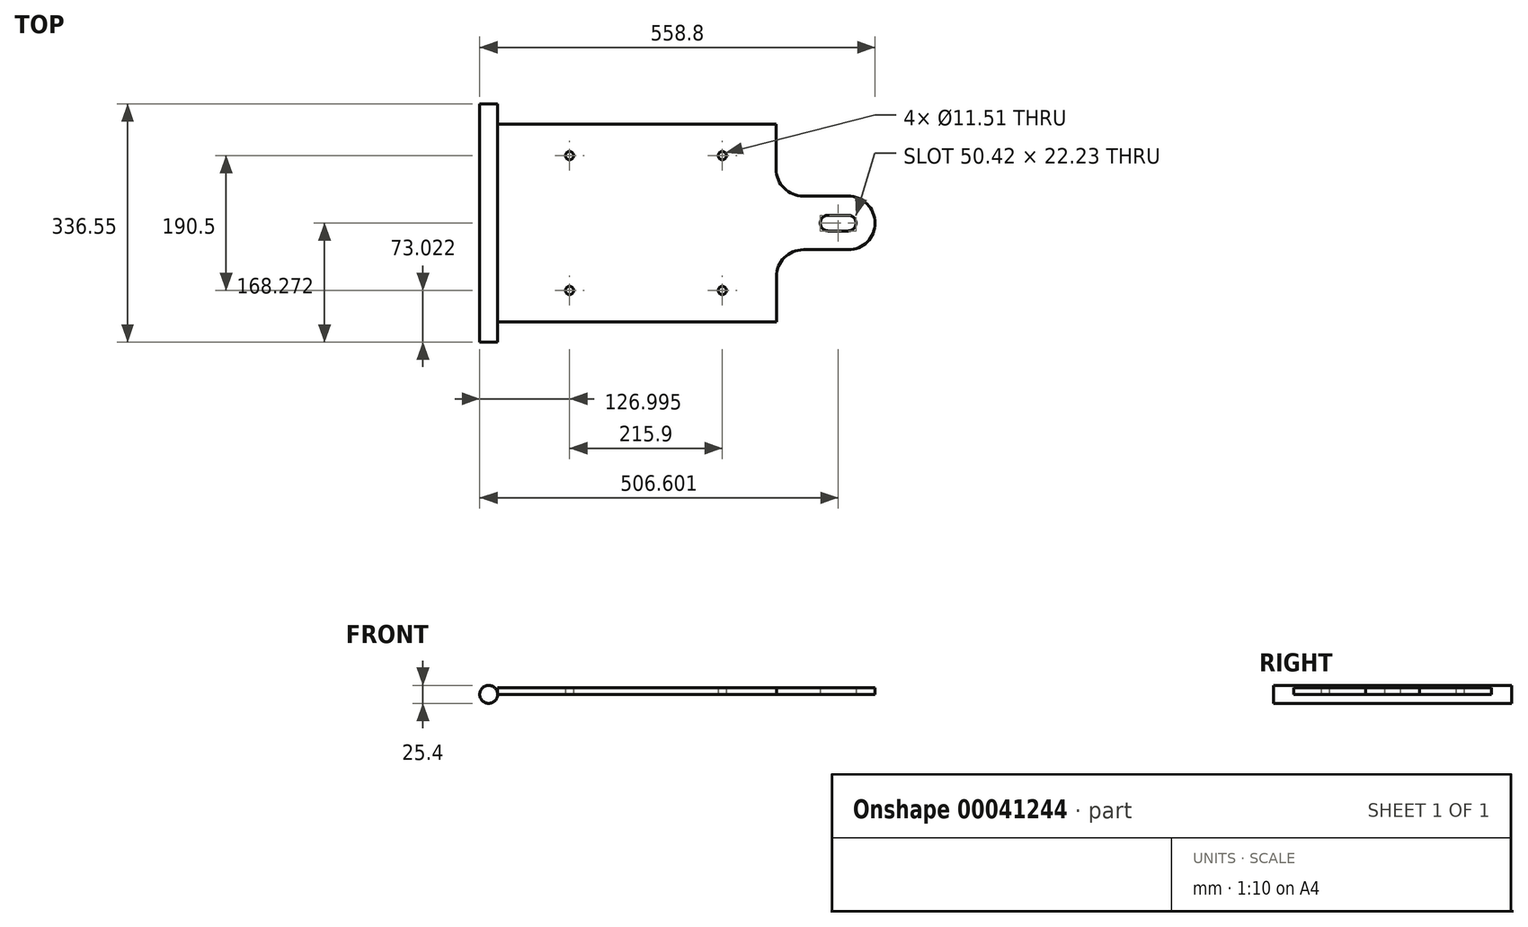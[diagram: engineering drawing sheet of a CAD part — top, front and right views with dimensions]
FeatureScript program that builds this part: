
annotation { "Feature Type Name" : "Feature", "Feature Type Description" : "" }
export const myFeature = defineFeature(function(context is Context, id is Id, definition is map)
    precondition{}
    {
        {
            var Q0;
            Q0=qCreatedBy(makeId("Top.planeOp"),FACE);
            var sketch = newSketch(context, id + "F0", { "sketchPlane" : qUnion([Q0])});
            skLineSegment(sketch, "E0.bottom", {"start": v(-236.93, 236.13) * mm, "end": v(156.77, 236.13) * mm});
            skLineSegment(sketch, "E0.top", {"start": v(-236.93, -43.27) * mm, "end": v(157.15, -43.27) * mm});
            skLineSegment(sketch, "E0.left", {"start": v(-236.93, 236.13) * mm, "end": v(-236.93, -43.27) * mm});
            skLineSegment(sketch, "E1", {"start": v(-236.93, 96.43) * mm, "end": v(296.47, 96.43) * mm, "construction": true});
            skPoint(sketch, "E1.startSnap0", {"position": v(-236.93, 96.43) * mm});
            skLineSegment(sketch, "E2", {"start": v(-236.93, 236.13) * mm, "end": v(-135.33, 236.13) * mm});
            skLineSegment(sketch, "E3", {"start": v(-135.33, 236.13) * mm, "end": v(80.57, 236.13) * mm, "construction": true});
            skLineSegment(sketch, "E4", {"start": v(-135.33, 236.13) * mm, "end": v(80.57, 236.13) * mm});
            skLineSegment(sketch, "E5.rect.bottom", {"start": v(80.57, 1.18) * mm, "end": v(-135.33, 1.18) * mm, "construction": true});
            skLineSegment(sketch, "E5.rect.top", {"start": v(80.57, 191.68) * mm, "end": v(-135.33, 191.68) * mm, "construction": true});
            skLineSegment(sketch, "E5.rect.left", {"start": v(80.57, 1.18) * mm, "end": v(80.57, 191.68) * mm, "construction": true});
            skLineSegment(sketch, "E5.rect.right", {"start": v(-135.33, 1.18) * mm, "end": v(-135.33, 191.68) * mm, "construction": true});
            skPoint(sketch, "E5.rect.middle", {"position": v(-27.38, 96.43) * mm});
            skLineSegment(sketch, "E6", {"start": v(156.77, 236.13) * mm, "end": v(156.77, 172.63) * mm});
            skLineSegment(sketch, "E7.rect.bottom", {"start": v(194.87, 134.53) * mm, "end": v(258.37, 134.53) * mm});
            skLineSegment(sketch, "E7.rect.top", {"start": v(195.25, 58.72) * mm, "end": v(258.75, 58.72) * mm});
            skLineSegment(sketch, "E8", {"start": v(-135.33, 191.68) * mm, "end": v(-135.33, 236.13) * mm, "construction": true});
            skLineSegment(sketch, "E9", {"start": v(-135.33, 1.18) * mm, "end": v(-135.33, -43.27) * mm, "construction": true});
            skArc(sketch, "E10.filletArc", {"start": v(156.77, 172.63) * mm, "mid": v(167.92, 145.7) * mm, "end": v(194.87, 134.53) * mm});
            skLineSegment(sketch, "E11", {"start": v(157.15, 20.62) * mm, "end": v(157.15, -43.27) * mm});
            skArc(sketch, "E12.filletArc", {"start": v(195.25, 58.72) * mm, "mid": v(168.3, 47.56) * mm, "end": v(157.15, 20.62) * mm});
            skLineSegment(sketch, "E13", {"start": v(296.47, 96.43) * mm, "end": v(296.47, 96.43) * mm});
            skArc(sketch, "E14.filletArc", {"start": v(296.47, 96.43) * mm, "mid": v(285.3, 123.37) * mm, "end": v(258.37, 134.53) * mm});
            skArc(sketch, "E15.filletArc", {"start": v(258.75, 58.72) * mm, "mid": v(285.42, 69.76) * mm, "end": v(296.47, 96.43) * mm});
            skLineSegment(sketch, "E16", {"start": v(258.37, 96.43) * mm, "end": v(230.18, 96.43) * mm});
            skArc(sketch, "E17.0.startCap", {"start": v(258.37, 107.54) * mm, "mid": v(269.48, 96.43) * mm, "end": v(258.37, 85.32) * mm});
            skArc(sketch, "E17.0.endCap", {"start": v(230.18, 85.32) * mm, "mid": v(219.06, 96.43) * mm, "end": v(230.18, 107.54) * mm});
            skLineSegment(sketch, "E17.0.left", {"start": v(258.37, 85.32) * mm, "end": v(230.18, 85.32) * mm});
            skLineSegment(sketch, "E17.0.right", {"start": v(258.37, 107.54) * mm, "end": v(230.18, 107.54) * mm});
            skPoint(sketch, "E18", {"position": v(296.47, 96.43) * mm});
            skSolve(sketch);
        }
        {
            var Q0;
            Q0=makeQuery(id+"F0.imprint","IMPRINT",FACE,{"disambiguationData":[TD([[makeQuery(id+"F0.imprint","IMPRINT",EDGE,{"derivedFrom":sQuery(id+"F0.wireOp",EDGE,"E0.bottom")}),-1.0]])]});
            extrude(context, id + "F1", {"entities" : qUnion([Q0]), "depth" : 9.52 * mm});
        }
        {
            var Q0;
            Q0=sQuery(id+"F0.wireOp",VERTEX,"E5.rect.right.end");
            var Q1;
            Q1=sQuery(id+"F0.wireOp",VERTEX,"E5.rect.top.start");
            var Q2;
            Q2=sQuery(id+"F0.wireOp",VERTEX,"E5.rect.bottom.start");
            var Q3;
            Q3=sQuery(id+"F0.wireOp",VERTEX,"E5.rect.bottom.end");
            var Q4;
            Q4=makeQuery(id+"F1.opExtrude","SWEPT_BODY",BODY,{"disambiguationData":[OSD([sQuery(id+"F0.wireOp",EDGE,"E0.bottom"),sQuery(id+"F0.wireOp",EDGE,"E0.top"),sQuery(id+"F0.wireOp",EDGE,"E0.left"),sQuery(id+"F0.wireOp",EDGE,"E0.right"),sQuery(id+"F0.wireOp",EDGE,"E2"),sQuery(id+"F0.wireOp",EDGE,"E4")])]});
            hole(context, id + "F2", {"style" : HoleStyle.SIMPLE, "holeDiameter" : 11.5 * mm, "endStyle" : HoleEndStyle.THROUGH, "oppositeDirection" : true, "locations" : qUnion([Q0, Q1, Q2, Q3]), "scope" : qUnion([Q4])});
        }
        {
            var Q0;
            Q0=makeQuery(id+"F1.opExtrude","SWEPT_FACE",FACE,{"disambiguationData":[OSD([sQuery(id+"F0.wireOp",EDGE,"E0.top")])]});
            var sketch = newSketch(context, id + "F3", { "sketchPlane" : qUnion([Q0])});
            skCircle(sketch, "E19", {"center": v(-249.63, 0) * mm, "radius": 12.7 * mm});
            skLineSegment(sketch, "E20", {"start": v(-249.63, 40.4) * mm, "end": v(-249.63, -62.23) * mm, "construction": true});
            skLineSegment(sketch, "E21.rect.bottom", {"start": v(-279.96, -44.45) * mm, "end": v(-219.31, -44.45) * mm});
            skLineSegment(sketch, "E21.rect.top", {"start": v(-279.96, 44.45) * mm, "end": v(-219.31, 44.45) * mm});
            skLineSegment(sketch, "E21.rect.left", {"start": v(-279.96, -44.45) * mm, "end": v(-279.96, 44.45) * mm});
            skLineSegment(sketch, "E21.rect.right", {"start": v(-219.31, -44.45) * mm, "end": v(-219.31, 44.45) * mm});
            skSolve(sketch);
        }
        {
            var Q0;
            Q0=makeQuery(id+"F3.imprint","IMPRINT",FACE,{"disambiguationData":[TD([[makeQuery(id+"F3.imprint","IMPRINT",EDGE,{"derivedFrom":sQuery(id+"F3.wireOp",EDGE,"E19")}),1.0]])]});
            var Q1;
            Q1=makeQuery(id+"F1.opExtrude","SWEPT_FACE",FACE,{"disambiguationData":[OSD([sQuery(id+"F0.wireOp",EDGE,"E0.bottom"),sQuery(id+"F0.wireOp",EDGE,"E2"),sQuery(id+"F0.wireOp",EDGE,"E4")])]});
            extrude(context, id + "F4", {"entities" : qUnion([Q0]), "endBound" : BoundingType.UP_TO_SURFACE, "oppositeDirection" : true, "endBoundEntityFace" : qUnion([Q1]), "depth" : 25.4 * mm});
        }
        {
            var Q0;
            Q0=makeQuery(id+"F4.opExtrude","CAP_FACE",FACE,{"disambiguationData":[OSD([sQuery(id+"F3.wireOp",EDGE,"E19")])],"isStart":true});
            extrude(context, id + "F5", {"entities" : qUnion([Q0]), "operationType" : NewBodyOperationType.ADD, "depth" : 28.57 * mm});
        }
        {
            var Q0;
            Q0=makeQuery(id+"F4.opExtrude","CAP_FACE",FACE,{"disambiguationData":[OSD([sQuery(id+"F3.wireOp",EDGE,"E19")])],"isStart":false});
            extrude(context, id + "F6", {"entities" : qUnion([Q0]), "operationType" : NewBodyOperationType.ADD, "depth" : 28.57 * mm});
        }
    });
